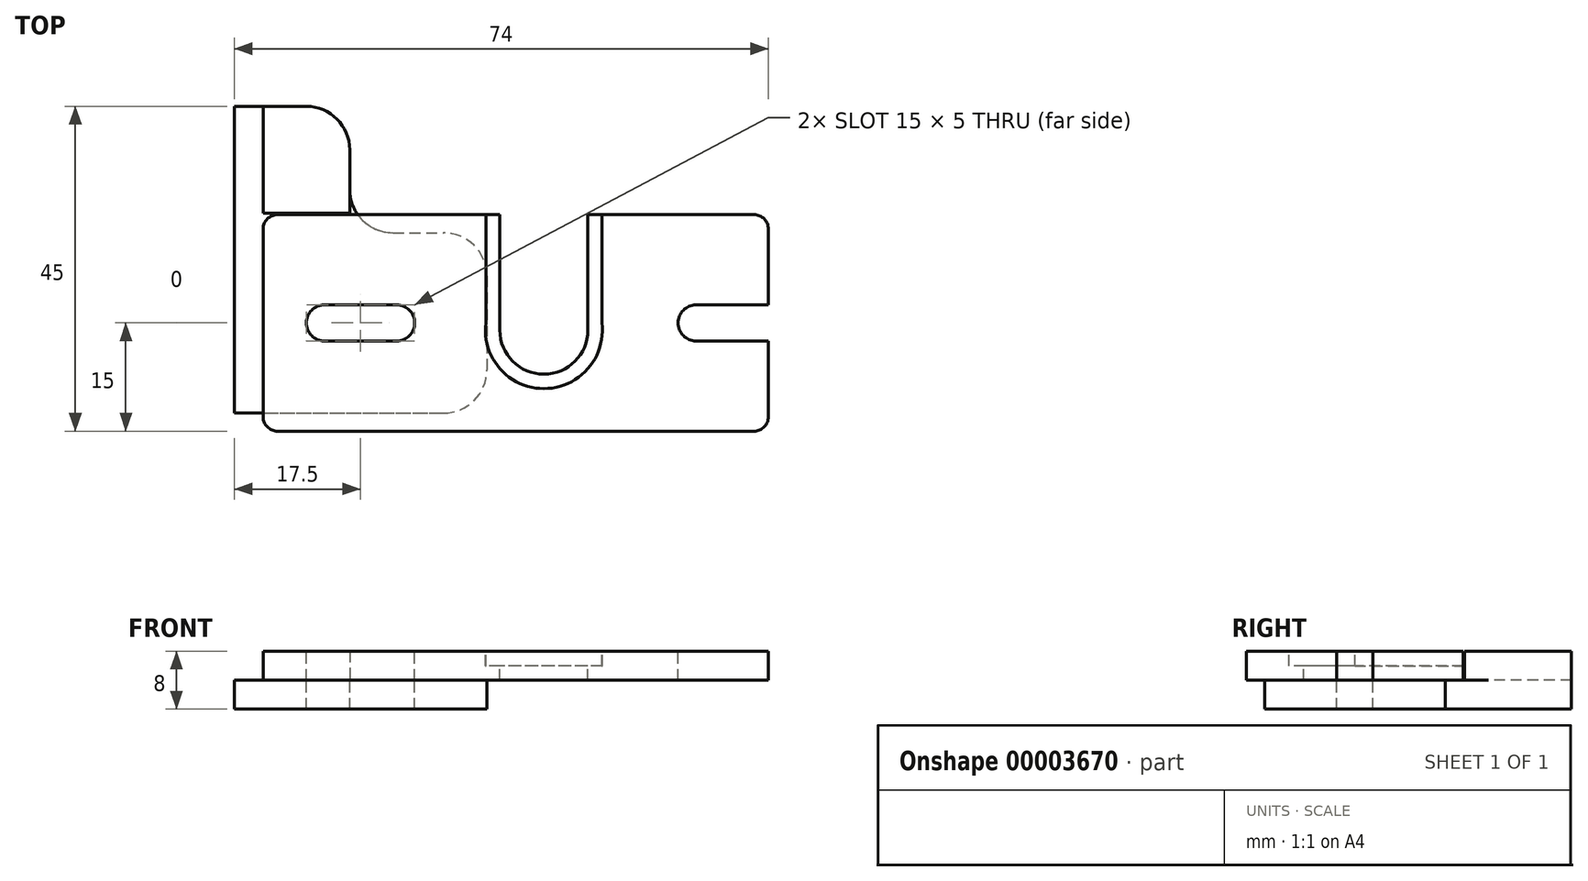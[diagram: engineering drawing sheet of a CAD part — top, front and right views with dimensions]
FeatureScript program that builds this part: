
annotation { "Feature Type Name" : "Feature", "Feature Type Description" : "" }
export const myFeature = defineFeature(function(context is Context, id is Id, definition is map)
    precondition{}
    {
        {
            var Q0;
            Q0=qCreatedBy(makeId("Top.planeOp"),FACE);
            var sketch = newSketch(context, id + "F0", { "sketchPlane" : qUnion([Q0])});
            skLineSegment(sketch, "E0.bottom", {"start": v(-103, 15) * mm, "end": v(-37, 15) * mm});
            skLineSegment(sketch, "E0.top", {"start": v(-103, -15) * mm, "end": v(-37, -15) * mm});
            skLineSegment(sketch, "E0.left", {"start": v(-105, 13) * mm, "end": v(-105, -13) * mm});
            skLineSegment(sketch, "E0.right", {"start": v(-35, 13) * mm, "end": v(-35, -13) * mm});
            skPoint(sketch, "E1.visualSharp", {"position": v(-105, -15) * mm});
            skArc(sketch, "E1.filletArc", {"start": v(-105, -13) * mm, "mid": v(-104.41, -14.41) * mm, "end": v(-103, -15) * mm});
            skPoint(sketch, "E2.visualSharp", {"position": v(-105, 15) * mm});
            skArc(sketch, "E2.filletArc", {"start": v(-103, 15) * mm, "mid": v(-104.41, 14.41) * mm, "end": v(-105, 13) * mm});
            skPoint(sketch, "E3.visualSharp", {"position": v(-35, 15) * mm});
            skArc(sketch, "E3.filletArc", {"start": v(-35, 13) * mm, "mid": v(-35.59, 14.41) * mm, "end": v(-37, 15) * mm});
            skPoint(sketch, "E4.visualSharp", {"position": v(-35, -15) * mm});
            skArc(sketch, "E4.filletArc", {"start": v(-37, -15) * mm, "mid": v(-35.59, -14.41) * mm, "end": v(-35, -13) * mm});
            skSolve(sketch);
        }
        {
            var Q0;
            Q0 = qSketchRegion(id + "F0", true);
            extrude(context, id + "F1", {"entities" : qUnion([Q0]), "depth" : 4 * mm});
        }
        {
            var Q0;
            Q0=makeQuery(id+"F1.opExtrude","CAP_FACE",FACE,{"disambiguationData":[OSD([sQuery(id+"F0.wireOp",EDGE,"E0.bottom"),sQuery(id+"F0.wireOp",EDGE,"E0.top"),sQuery(id+"F0.wireOp",EDGE,"E0.left"),sQuery(id+"F0.wireOp",EDGE,"E0.right"),sQuery(id+"F0.wireOp",EDGE,"E1.filletArc"),sQuery(id+"F0.wireOp",EDGE,"E2.filletArc"),sQuery(id+"F0.wireOp",EDGE,"E3.filletArc"),sQuery(id+"F0.wireOp",EDGE,"E4.filletArc")])],"isStart":false});
            var sketch = newSketch(context, id + "F2", { "sketchPlane" : qUnion([Q0])});
            skCircle(sketch, "E5", {"center": v(-95, 0) * mm, "radius": 2.5 * mm});
            skCircle(sketch, "E6", {"center": v(-53.5, 0) * mm, "radius": 2.5 * mm});
            skLineSegment(sketch, "E7.bottom", {"start": v(-105, 2.5) * mm, "end": v(-95, 2.5) * mm});
            skLineSegment(sketch, "E7.top", {"start": v(-105, -2.5) * mm, "end": v(-95, -2.5) * mm});
            skLineSegment(sketch, "E7.left", {"start": v(-105, 2.5) * mm, "end": v(-105, -2.5) * mm});
            skCircle(sketch, "E8", {"center": v(-43.5, 0) * mm, "radius": 2.5 * mm});
            skLineSegment(sketch, "E9", {"start": v(-53.5, 2.5) * mm, "end": v(-43.5, 2.5) * mm});
            skLineSegment(sketch, "E10", {"start": v(-43.5, -2.5) * mm, "end": v(-53.5, -2.5) * mm});
            skCircle(sketch, "E11", {"center": v(-73.9, -1) * mm, "radius": 6.1 * mm});
            skLineSegment(sketch, "E12", {"start": v(-80, -1) * mm, "end": v(-80, 15) * mm});
            skLineSegment(sketch, "E13", {"start": v(-67.8, -1) * mm, "end": v(-67.8, 15) * mm});
            skLineSegment(sketch, "E14", {"start": v(-67.8, 15) * mm, "end": v(-80, 15) * mm});
            skSolve(sketch);
        }
        {
            var Q0;
            Q0 = qSketchRegion(id + "F2", true);
            extrude(context, id + "F3", {"entities" : qUnion([Q0]), "operationType" : NewBodyOperationType.REMOVE, "endBound" : BoundingType.THROUGH_ALL, "oppositeDirection" : true, "depth" : 25 * mm});
        }
        {
            var Q0;
            Q0=makeQuery(id+"F1.opExtrude","CAP_FACE",FACE,{"disambiguationData":[OSD([sQuery(id+"F0.wireOp",EDGE,"E0.bottom"),sQuery(id+"F0.wireOp",EDGE,"E0.top"),sQuery(id+"F0.wireOp",EDGE,"E0.left"),sQuery(id+"F0.wireOp",EDGE,"E0.right"),sQuery(id+"F0.wireOp",EDGE,"E1.filletArc"),sQuery(id+"F0.wireOp",EDGE,"E2.filletArc"),sQuery(id+"F0.wireOp",EDGE,"E3.filletArc"),sQuery(id+"F0.wireOp",EDGE,"E4.filletArc")])],"isStart":false});
            var sketch = newSketch(context, id + "F4", { "sketchPlane" : qUnion([Q0])});
            skCircle(sketch, "E15", {"center": v(-73.9, -1) * mm, "radius": 8.1 * mm});
            skLineSegment(sketch, "E16", {"start": v(-81.94, 0) * mm, "end": v(-81.94, 15) * mm});
            skLineSegment(sketch, "E17", {"start": v(-65.86, 0) * mm, "end": v(-65.86, 15) * mm});
            skLineSegment(sketch, "E18", {"start": v(-65.86, 15) * mm, "end": v(-81.94, 15) * mm});
            skSolve(sketch);
        }
        {
            var Q0;
            Q0 = qSketchRegion(id + "F4", true);
            extrude(context, id + "F5", {"entities" : qUnion([Q0]), "operationType" : NewBodyOperationType.REMOVE, "oppositeDirection" : true, "depth" : 2 * mm});
        }
        {
            var Q0;
            Q0=makeQuery(id+"F1.opExtrude","SWEPT_BODY",BODY,{"disambiguationData":[OSD([sQuery(id+"F0.wireOp",EDGE,"E0.bottom"),sQuery(id+"F0.wireOp",EDGE,"E0.top"),sQuery(id+"F0.wireOp",EDGE,"E0.left"),sQuery(id+"F0.wireOp",EDGE,"E0.right"),sQuery(id+"F0.wireOp",EDGE,"E1.filletArc"),sQuery(id+"F0.wireOp",EDGE,"E2.filletArc"),sQuery(id+"F0.wireOp",EDGE,"E3.filletArc"),sQuery(id+"F0.wireOp",EDGE,"E4.filletArc")])]});
            var Q1;
            Q1=makeQuery(id+"F1.opExtrude","SWEPT_FACE",FACE,{"disambiguationData":[OSD([sQuery(id+"F0.wireOp",EDGE,"E0.right")])]});
            mirror(context, id + "F6", {"entities" : qUnion([Q0]), "mirrorPlane" : qUnion([Q1])});
        }
        {
            var Q0;
            Q0=makeQuery(id+"F1.opExtrude","SWEPT_BODY",BODY,{"disambiguationData":[OSD([sQuery(id+"F0.wireOp",EDGE,"E0.bottom"),sQuery(id+"F0.wireOp",EDGE,"E0.top"),sQuery(id+"F0.wireOp",EDGE,"E0.left"),sQuery(id+"F0.wireOp",EDGE,"E0.right"),sQuery(id+"F0.wireOp",EDGE,"E1.filletArc"),sQuery(id+"F0.wireOp",EDGE,"E2.filletArc"),sQuery(id+"F0.wireOp",EDGE,"E3.filletArc"),sQuery(id+"F0.wireOp",EDGE,"E4.filletArc")])]});
            deleteBodies(context, id + "F7", {"entities" : qUnion([Q0])});
        }
        {
            var Q0;
            Q0=makeQuery(id+"F6.opPattern","COPY",FACE,{"derivedFrom":makeQuery(id+"F1.opExtrude","CAP_FACE",FACE,{"disambiguationData":[OSD([sQuery(id+"F0.wireOp",EDGE,"E0.bottom"),sQuery(id+"F0.wireOp",EDGE,"E0.top"),sQuery(id+"F0.wireOp",EDGE,"E0.left"),sQuery(id+"F0.wireOp",EDGE,"E0.right"),sQuery(id+"F0.wireOp",EDGE,"E1.filletArc"),sQuery(id+"F0.wireOp",EDGE,"E2.filletArc"),sQuery(id+"F0.wireOp",EDGE,"E3.filletArc"),sQuery(id+"F0.wireOp",EDGE,"E4.filletArc")])],"isStart":true}),"instanceName":"1"});
            var sketch = newSketch(context, id + "F8", { "sketchPlane" : qUnion([Q0])});
            skLineSegment(sketch, "E19", {"start": v(-23, -24) * mm, "end": v(-23, -18.5) * mm});
            skLineSegment(sketch, "E20", {"start": v(-17, -12.5) * mm, "end": v(-10, -12.5) * mm});
            skLineSegment(sketch, "E21", {"start": v(-4, -6.5) * mm, "end": v(-4, 6.5) * mm});
            skPoint(sketch, "E22.visualSharp", {"position": v(-4, 12.5) * mm});
            skArc(sketch, "E22.filletArc", {"start": v(-4, 6.5) * mm, "mid": v(-5.76, 10.74) * mm, "end": v(-10, 12.5) * mm});
            skPoint(sketch, "E23.visualSharp", {"position": v(-4, -12.5) * mm});
            skArc(sketch, "E23.filletArc", {"start": v(-10, -12.5) * mm, "mid": v(-5.76, -10.74) * mm, "end": v(-4, -6.5) * mm});
            skPoint(sketch, "E24.visualSharp", {"position": v(-23, -12.5) * mm});
            skArc(sketch, "E24.filletArc", {"start": v(-17, -12.5) * mm, "mid": v(-21.24, -14.26) * mm, "end": v(-23, -18.5) * mm});
            skPoint(sketch, "E25.visualSharp", {"position": v(-23, -30) * mm});
            skArc(sketch, "E25.filletArc", {"start": v(-29, -30) * mm, "mid": v(-24.76, -28.24) * mm, "end": v(-23, -24) * mm});
            skCircle(sketch, "E26", {"center": v(-26.5, 0) * mm, "radius": 2.5 * mm});
            skCircle(sketch, "E27", {"center": v(-16.5, 0) * mm, "radius": 2.5 * mm});
            skLineSegment(sketch, "E28", {"start": v(-26.5, 2.5) * mm, "end": v(-16.5, 2.5) * mm});
            skLineSegment(sketch, "E29", {"start": v(-16.5, -2.5) * mm, "end": v(-26.5, -2.5) * mm});
            skLineSegment(sketch, "E30", {"start": v(-39, 12.5) * mm, "end": v(-39, -30) * mm});
            skLineSegment(sketch, "E31", {"start": v(-39, -30) * mm, "end": v(-29, -30) * mm});
            skLineSegment(sketch, "E32", {"start": v(-39, 12.5) * mm, "end": v(-10, 12.5) * mm});
            skSolve(sketch);
        }
        {
            var Q0;
            Q0 = qSketchRegion(id + "F8", true);
            extrude(context, id + "F9", {"entities" : qUnion([Q0]), "depth" : 4 * mm});
        }
        {
            var Q0;
            Q0=makeQuery(id+"F9.opExtrude","CAP_FACE",FACE,{"disambiguationData":[OSD([sQuery(id+"F8.wireOp",EDGE,"8ad73940-a8ad-4a60-a6d9-fb6aa6c1050e"),sQuery(id+"F8.wireOp",EDGE,"ad5d0125-e347-4301-922b-63e8063ffe04"),sQuery(id+"F8.wireOp",EDGE,"E19"),sQuery(id+"F8.wireOp",EDGE,"E20"),sQuery(id+"F8.wireOp",EDGE,"E21"),sQuery(id+"F8.wireOp",EDGE,"a01ea1b8-4455-41e5-96ba-e2f11eac1cd2"),sQuery(id+"F8.wireOp",EDGE,"E22.filletArc"),sQuery(id+"F8.wireOp",EDGE,"E23.filletArc"),sQuery(id+"F8.wireOp",EDGE,"E24.filletArc"),sQuery(id+"F8.wireOp",EDGE,"E25.filletArc"),sQuery(id+"F8.wireOp",EDGE,"E26"),sQuery(id+"F8.wireOp",EDGE,"E27"),sQuery(id+"F8.wireOp",EDGE,"E28"),sQuery(id+"F8.wireOp",EDGE,"E29")])],"isStart":true});
            var sketch = newSketch(context, id + "F10", { "sketchPlane" : qUnion([Q0])});
            skLineSegment(sketch, "E33.bottom", {"start": v(-35, 30) * mm, "end": v(-29, 30) * mm});
            skLineSegment(sketch, "E33.top", {"start": v(-35, 15.2) * mm, "end": v(-23, 15.2) * mm});
            skLineSegment(sketch, "E33.left", {"start": v(-35, 30) * mm, "end": v(-35, 15.2) * mm});
            skLineSegment(sketch, "E33.right", {"start": v(-23, 24) * mm, "end": v(-23, 15.2) * mm});
            skPoint(sketch, "E34.visualSharp", {"position": v(-23, 30) * mm});
            skArc(sketch, "E34.filletArc", {"start": v(-23, 24) * mm, "mid": v(-24.76, 28.24) * mm, "end": v(-29, 30) * mm});
            skSolve(sketch);
        }
        {
            var Q0;
            Q0 = qSketchRegion(id + "F10", true);
            extrude(context, id + "F11", {"entities" : qUnion([Q0]), "operationType" : NewBodyOperationType.ADD, "depth" : 4 * mm});
        }
    });
